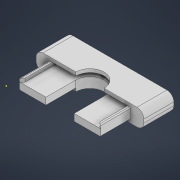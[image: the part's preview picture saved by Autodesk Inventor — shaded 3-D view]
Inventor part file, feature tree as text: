
AUTODESK INVENTOR PART (.ipt)
format: ipt  version: 2022 (Build 260153000, 153)  size: 484,864 bytes
history: native  units: mm
features: sketch x11, extrude x8, fillet x3, emboss x1
ambient origin geometry x8: Origin, YZ Plane, XZ Plane, XY Plane, X Axis, Y Axis, Z Axis, Center Point
bodies: Body1 (feature_tree)
feature tree (23):
  extrude  "Extrusion8"  Depth=10.0mm
  extrude  "Extrusion9"  Depth=17.5mm
  extrude  "Extrusion10"  Depth=35.0mm TaperAngle=0.0deg
  extrude  "Extrusion11"  Depth=17.5mm
  extrude  "Extrusion12"  Depth=2.0mm TaperAngle=0.0deg
  fillet  "Fillet5"  Radius=33.0mm
  extrude  "Extrusion13"  Depth=17.5mm
  fillet  "Fillet6"  Radius=17.5mm
  emboss  "Emboss3"
  sketch  "Sketch22"  dims[d64=0.2mm d65=0.0mm d66=0.2mm d67=0.0mm d68=2.0mm]
  extrude  "Extrusion14"  Depth=1.0mm TaperAngle=0.0deg
  extrude  "Extrusion15"  Depth=0.2mm TaperAngle=0.0deg
  fillet  "Fillet7"  Radius=2.0mm
  sketch  "Sketch25"
  sketch  "Sketch13"  dims[d38=63.0mm d39=10.0mm]
  sketch  "Sketch15"  dims[d40=35.0mm d41=0.0mm d42=17.5mm]
  sketch  "Sketch16"  dims[d43=16.5mm d44=35.0mm d45=0.0mm]
  sketch  "Sketch17"  dims[d46=63.0mm d47=17.5mm]
  sketch  "Sketch19"  dims[d48=2.0mm d49=0.0mm d51=2.0mm d52=0.0mm d55=33.0mm d56=0.0mm]
  sketch  "Sketch20"  dims[d57=2.0mm d58=48.0mm d59=17.5mm d60=0.0mm]
  sketch  "Sketch21"  dims[d61=1.0mm d62=1.0mm d63=0.0mm]
  sketch  "Sketch23"  dims[d69=4.0mm]
  sketch  "Sketch24"  dims[d70=17.5mm]
